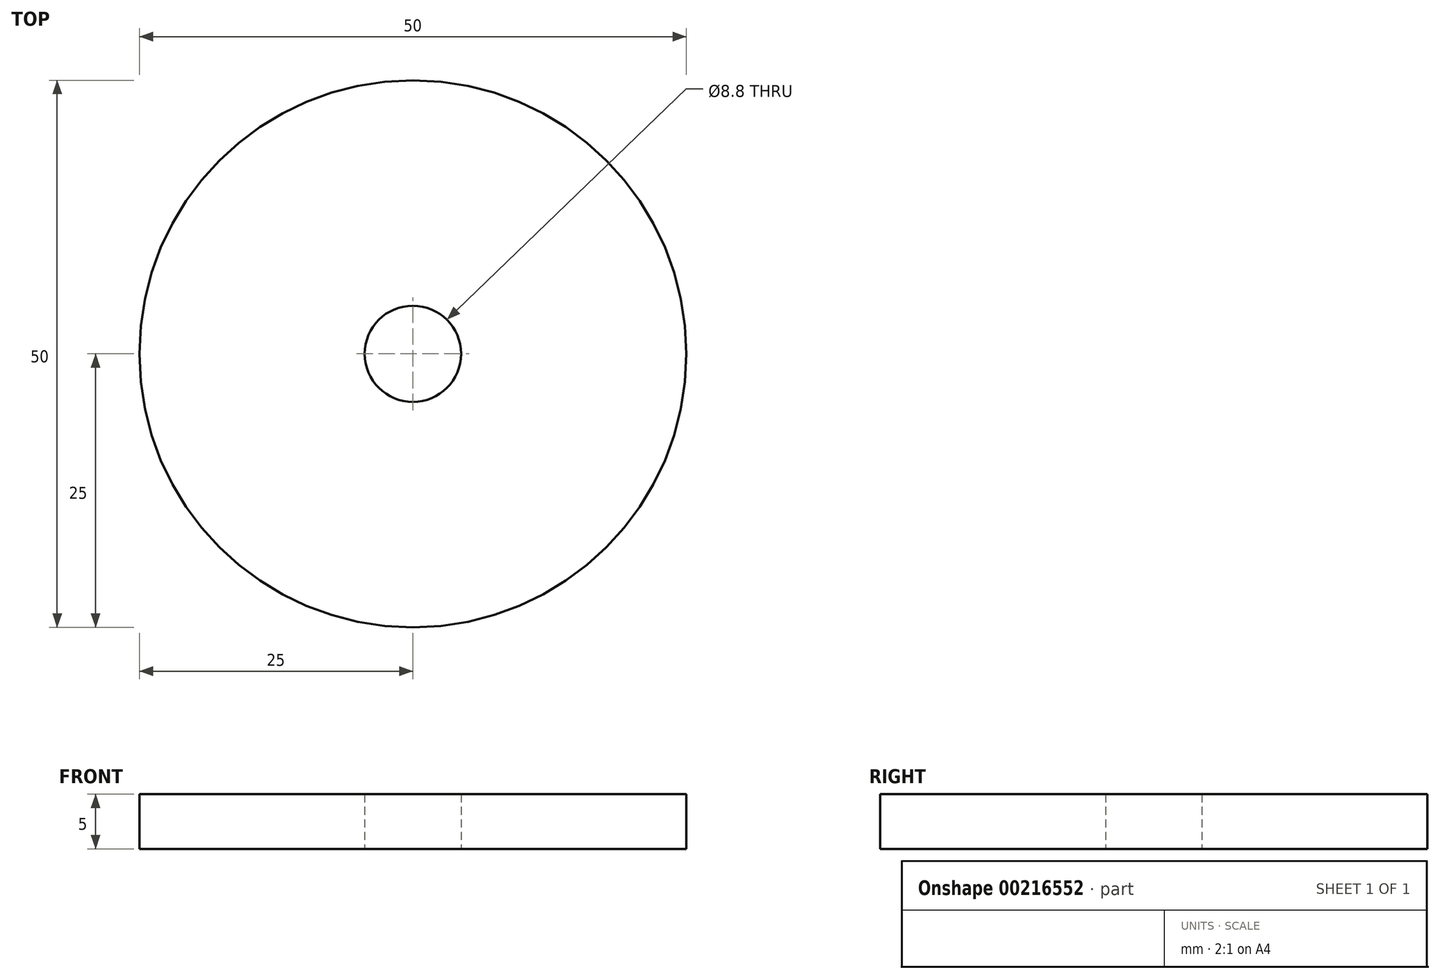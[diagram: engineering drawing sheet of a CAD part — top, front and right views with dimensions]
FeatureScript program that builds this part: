
annotation { "Feature Type Name" : "Feature", "Feature Type Description" : "" }
export const myFeature = defineFeature(function(context is Context, id is Id, definition is map)
    precondition{}
    {
        {
            var Q0;
            Q0=qCreatedBy(makeId("Top.planeOp"),FACE);
            var sketch = newSketch(context, id + "F0", { "sketchPlane" : qUnion([Q0])});
            skCircle(sketch, "E0", {"center": v(0, 0) * mm, "radius": 25 * mm});
            skCircle(sketch, "E1", {"center": v(0, 0) * mm, "radius": 4.4 * mm});
            skSolve(sketch);
        }
        {
            var Q0;
            Q0=makeQuery(id+"F0.imprint","IMPRINT",FACE,{"disambiguationData":[TD([[makeQuery(id+"F0.imprint","IMPRINT",EDGE,{"derivedFrom":sQuery(id+"F0.wireOp",EDGE,"E0")}),1.0]])]});
            extrude(context, id + "F1", {"entities" : qUnion([Q0]), "depth" : 5 * mm});
        }
    });
